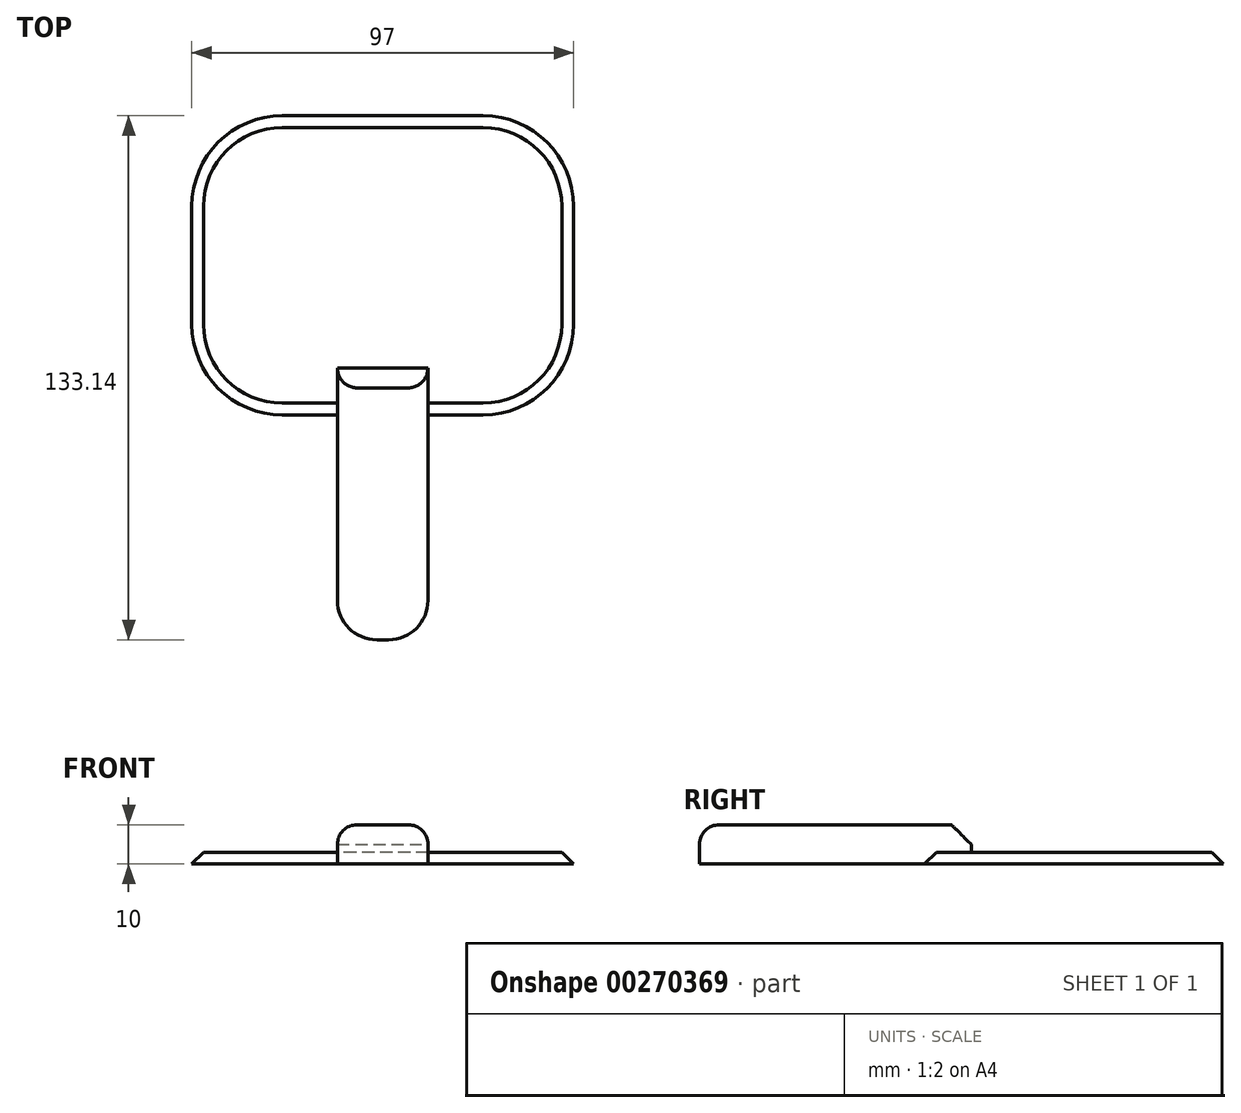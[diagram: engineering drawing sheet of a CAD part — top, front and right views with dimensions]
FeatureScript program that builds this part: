
annotation { "Feature Type Name" : "Feature", "Feature Type Description" : "" }
export const myFeature = defineFeature(function(context is Context, id is Id, definition is map)
    precondition{}
    {
        {
            var Q0;
            Q0=qCreatedBy(makeId("Top.planeOp"),FACE);
            var sketch = newSketch(context, id + "F0", { "sketchPlane" : qUnion([Q0])});
            skLineSegment(sketch, "E0.bottom", {"start": v(-50.5, -6.6) * mm, "end": v(50.5, -6.6) * mm});
            skLineSegment(sketch, "E0.top", {"start": v(-50.5, 73.4) * mm, "end": v(50.5, 73.4) * mm});
            skLineSegment(sketch, "E0.left", {"start": v(-50.5, -6.6) * mm, "end": v(-50.5, 73.4) * mm});
            skLineSegment(sketch, "E0.right", {"start": v(50.5, -6.6) * mm, "end": v(50.5, 73.4) * mm});
            skPoint(sketch, "E0.middle", {"position": v(0, 33.4) * mm});
            skSolve(sketch);
        }
        {
            var Q0;
            Q0=makeQuery(id+"F0.imprint","IMPRINT",FACE,{"disambiguationData":[TD([[makeQuery(id+"F0.imprint","IMPRINT",EDGE,{"derivedFrom":sQuery(id+"F0.wireOp",EDGE,"E0.bottom")}),1.0]])]});
            extrude(context, id + "F1", {"entities" : qUnion([Q0]), "depth" : 3 * mm});
        }
        {
            var Q0;
            Q0=makeQuery(id+"F1.opExtrude","SWEPT_EDGE",EDGE,{"disambiguationData":[OSD([sQuery(id+"F0.wireOp",EDGE,"E0.bottom"),sQuery(id+"F0.wireOp",EDGE,"E0.right")])]});
            var Q1;
            Q1=makeQuery(id+"F1.opExtrude","SWEPT_EDGE",EDGE,{"disambiguationData":[OSD([sQuery(id+"F0.wireOp",EDGE,"E0.top"),sQuery(id+"F0.wireOp",EDGE,"E0.right")])]});
            var Q2;
            Q2=makeQuery(id+"F1.opExtrude","SWEPT_EDGE",EDGE,{"disambiguationData":[OSD([sQuery(id+"F0.wireOp",EDGE,"E0.bottom"),sQuery(id+"F0.wireOp",EDGE,"E0.left")])]});
            var Q3;
            Q3=makeQuery(id+"F1.opExtrude","SWEPT_EDGE",EDGE,{"disambiguationData":[OSD([sQuery(id+"F0.wireOp",EDGE,"E0.top"),sQuery(id+"F0.wireOp",EDGE,"E0.left")])]});
            fillet(context, id + "F2", {"entities" : qUnion([Q0, Q1, Q2, Q3]), "radius" : 25 * mm, "tangentPropagation" : true, "allowEdgeOverflow" : false});
        }
        {
            var Q0;
            Q0=qCreatedBy(makeId("Top.planeOp"),FACE);
            var sketch = newSketch(context, id + "F3", { "sketchPlane" : qUnion([Q0])});
            skLineSegment(sketch, "E1.bottom", {"start": v(-11.5, -61.74) * mm, "end": v(11.5, -61.74) * mm});
            skLineSegment(sketch, "E1.top", {"start": v(-11.5, 7.26) * mm, "end": v(11.5, 7.26) * mm});
            skLineSegment(sketch, "E1.left", {"start": v(-11.5, -61.74) * mm, "end": v(-11.5, 7.26) * mm});
            skLineSegment(sketch, "E1.right", {"start": v(11.5, -61.74) * mm, "end": v(11.5, 7.26) * mm});
            skPoint(sketch, "E1.middle", {"position": v(0, -27.24) * mm});
            skSolve(sketch);
        }
        {
            var Q0;
            Q0=makeQuery(id+"F3.imprint","IMPRINT",FACE,{"disambiguationData":[TD([[makeQuery(id+"F3.imprint","IMPRINT",EDGE,{"derivedFrom":sQuery(id+"F3.wireOp",EDGE,"E1.bottom")}),1.0]])]});
            extrude(context, id + "F4", {"entities" : qUnion([Q0]), "operationType" : NewBodyOperationType.ADD, "depth" : 10 * mm});
        }
        {
            var Q0;
            Q0=makeQuery(id+"F4.opExtrude","SWEPT_EDGE",EDGE,{"disambiguationData":[OSD([sQuery(id+"F3.wireOp",EDGE,"E1.bottom"),sQuery(id+"F3.wireOp",EDGE,"E1.right")])]});
            var Q1;
            Q1=makeQuery(id+"F4.opExtrude","SWEPT_EDGE",EDGE,{"disambiguationData":[OSD([sQuery(id+"F3.wireOp",EDGE,"E1.bottom"),sQuery(id+"F3.wireOp",EDGE,"E1.left")])]});
            fillet(context, id + "F5", {"entities" : qUnion([Q0, Q1]), "radius" : 10 * mm, "tangentPropagation" : true, "allowEdgeOverflow" : false});
        }
        {
            var Q0;
            Q0=makeQuery(id+"F4.opExtrude","CAP_EDGE",EDGE,{"disambiguationData":[OSD([sQuery(id+"F3.wireOp",EDGE,"E1.top")])],"isStart":false});
            chamfer(context, id + "F6", {"entities" : qUnion([Q0]), "width" : 5 * mm, "tangentPropagation" : true});
        }
        {
            var Q0;
            Q0=makeQuery(id+"F4.opExtrude","CAP_EDGE",EDGE,{"disambiguationData":[OSD([sQuery(id+"F3.wireOp",EDGE,"E1.left")])],"isStart":false});
            fillet(context, id + "F7", {"entities" : qUnion([Q0]), "radius" : 5 * mm, "tangentPropagation" : true, "allowEdgeOverflow" : false});
        }
        {
            var Q0;
            {var subQ0=sQuery(id+"F0.wireOp",EDGE,"E0.left");var subQ1=sQuery(id+"F0.wireOp",EDGE,"E0.top");Q0=makeQuery(id+"F2.opFillet","BLEND_EDGE",EDGE,{"blendedFrom":[makeQuery(id+"F1.opExtrude","SWEPT_EDGE",EDGE,{"disambiguationData":[OSD([subQ1,subQ0])]}),makeQuery(id+"F1.opExtrude","CAP_FACE",FACE,{"disambiguationData":[OSD([sQuery(id+"F0.wireOp",EDGE,"E0.bottom"),subQ1,subQ0,sQuery(id+"F0.wireOp",EDGE,"E0.right")])],"isStart":false})],"blendedInto":[makeQuery(id+"F1.opExtrude","CAP_FACE",FACE,{"disambiguationData":[OSD([sQuery(id+"F0.wireOp",EDGE,"E0.bottom"),subQ1,subQ0,sQuery(id+"F0.wireOp",EDGE,"E0.right")])],"isStart":false})]});}
            chamfer(context, id + "F8", {"entities" : qUnion([Q0]), "width" : 5 * mm, "tangentPropagation" : true});
        }
    });
